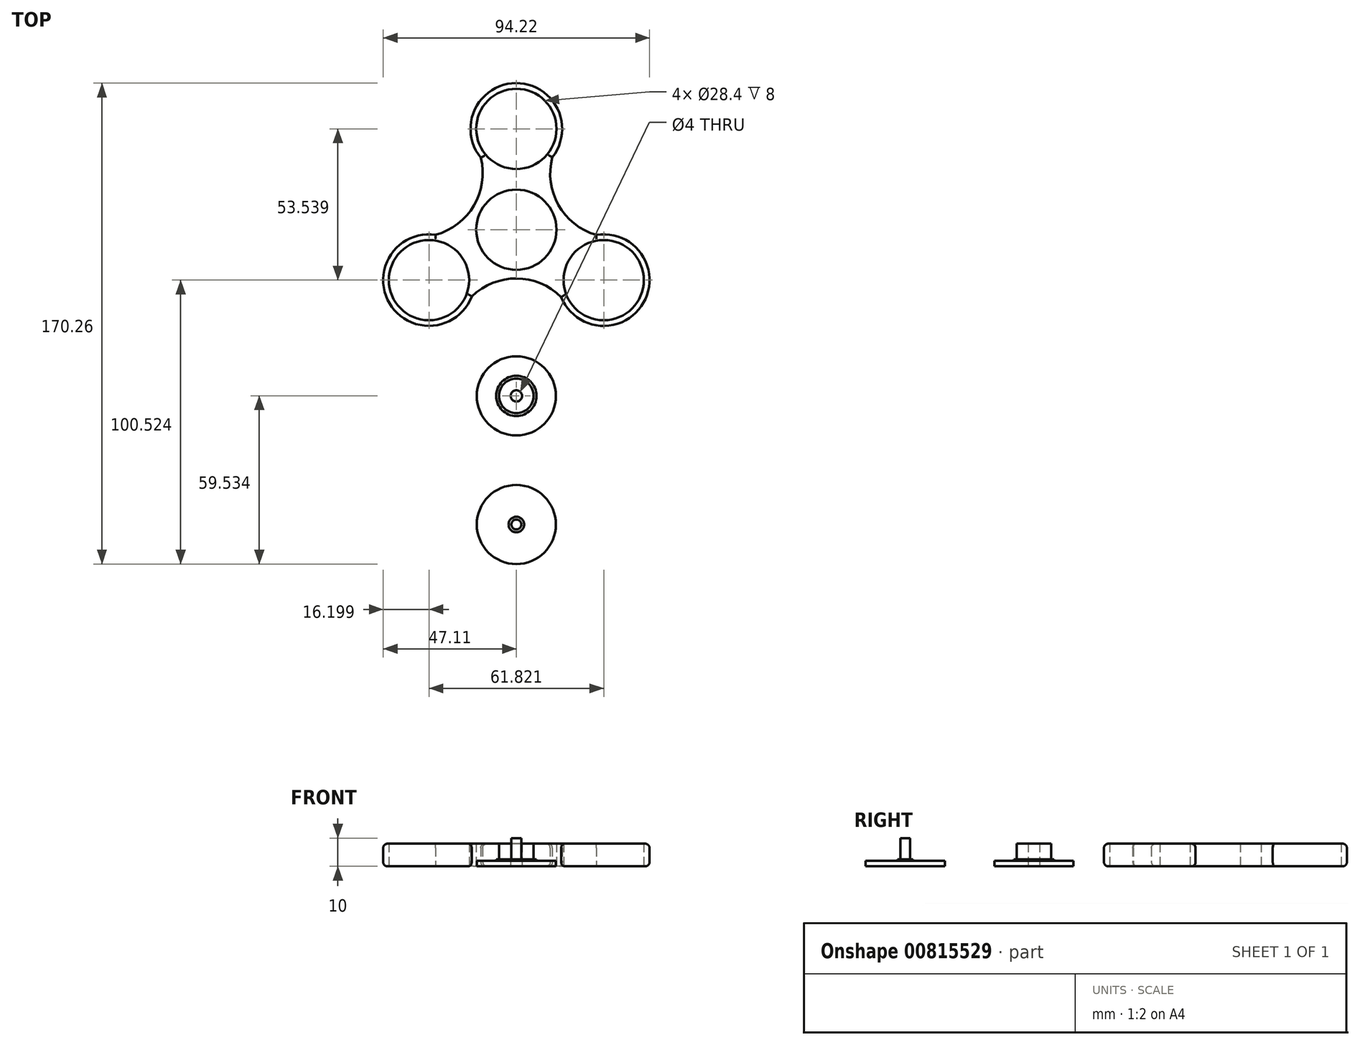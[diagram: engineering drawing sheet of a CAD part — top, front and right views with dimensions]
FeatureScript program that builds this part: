
annotation { "Feature Type Name" : "Feature", "Feature Type Description" : "" }
export const myFeature = defineFeature(function(context is Context, id is Id, definition is map)
    precondition{}
    {
        {
            var Q0;
            Q0=qCreatedBy(makeId("Top.planeOp"),FACE);
            var sketch = newSketch(context, id + "F0", { "sketchPlane" : qUnion([Q0])});
            skCircle(sketch, "E0", {"center": v(0, 0) * mm, "radius": 14.2 * mm});
            skCircle(sketch, "E1", {"center": v(0, 35.7) * mm, "radius": 14.2 * mm});
            skArc(sketch, "E2", {"start": v(12.73, 25.67) * mm, "mid": v(-0.12, 51.9) * mm, "end": v(-12.58, 25.49) * mm});
            skArc(sketch, "E3.1.0", {"start": v(-28.6, -1.81) * mm, "mid": v(-44.88, -26.05) * mm, "end": v(-15.78, -23.64) * mm});
            skCircle(sketch, "E3.1.1", {"center": v(-30.91, -17.85) * mm, "radius": 14.2 * mm});
            skArc(sketch, "E3.2.0", {"start": v(15.87, -23.86) * mm, "mid": v(45, -25.84) * mm, "end": v(28.36, -1.85) * mm});
            skCircle(sketch, "E3.2.1", {"center": v(30.91, -17.85) * mm, "radius": 14.2 * mm});
            skArc(sketch, "E4", {"start": v(15.87, -23.86) * mm, "mid": v(0.09, -17.27) * mm, "end": v(-15.78, -23.64) * mm});
            skArc(sketch, "E5.1.0", {"start": v(12.73, 25.67) * mm, "mid": v(14.9, 8.71) * mm, "end": v(28.36, -1.85) * mm});
            skArc(sketch, "E5.2.0", {"start": v(-28.6, -1.81) * mm, "mid": v(-15, 8.56) * mm, "end": v(-12.58, 25.49) * mm});
            skSolve(sketch);
        }
        {
            var Q0;
            Q0=qSketchRegion(id+"F0",true);
            extrude(context, id + "F1", {"entities" : qUnion([Q0]), "depth" : 8 * mm, "offsetDistance" : 25 * mm});
        }
        {
            var Q0;
            Q0=makeQuery(id+"F1.opExtrude","CAP_EDGE",EDGE,{"disambiguationData":[OSD([sQuery(id+"F0.wireOp",EDGE,"E3.1.0")])],"isStart":false});
            var Q1;
            Q1=makeQuery(id+"F1.opExtrude","CAP_EDGE",EDGE,{"disambiguationData":[OSD([sQuery(id+"F0.wireOp",EDGE,"E4")])],"isStart":false});
            var Q2;
            Q2=makeQuery(id+"F1.opExtrude","CAP_EDGE",EDGE,{"disambiguationData":[OSD([sQuery(id+"F0.wireOp",EDGE,"E3.2.0")])],"isStart":false});
            var Q3;
            Q3=makeQuery(id+"F1.opExtrude","CAP_EDGE",EDGE,{"disambiguationData":[OSD([sQuery(id+"F0.wireOp",EDGE,"E5.1.0")])],"isStart":false});
            var Q4;
            Q4=makeQuery(id+"F1.opExtrude","CAP_EDGE",EDGE,{"disambiguationData":[OSD([sQuery(id+"F0.wireOp",EDGE,"E2")])],"isStart":false});
            var Q5;
            Q5=makeQuery(id+"F1.opExtrude","CAP_EDGE",EDGE,{"disambiguationData":[OSD([sQuery(id+"F0.wireOp",EDGE,"E5.2.0")])],"isStart":false});
            var Q6;
            Q6=makeQuery(id+"F1.opExtrude","CAP_EDGE",EDGE,{"disambiguationData":[OSD([sQuery(id+"F0.wireOp",EDGE,"E4")])],"isStart":true});
            var Q7;
            Q7=makeQuery(id+"F1.opExtrude","CAP_EDGE",EDGE,{"disambiguationData":[OSD([sQuery(id+"F0.wireOp",EDGE,"E3.1.0")])],"isStart":true});
            var Q8;
            Q8=makeQuery(id+"F1.opExtrude","CAP_EDGE",EDGE,{"disambiguationData":[OSD([sQuery(id+"F0.wireOp",EDGE,"E5.2.0")])],"isStart":true});
            var Q9;
            Q9=makeQuery(id+"F1.opExtrude","CAP_EDGE",EDGE,{"disambiguationData":[OSD([sQuery(id+"F0.wireOp",EDGE,"E2")])],"isStart":true});
            var Q10;
            Q10=makeQuery(id+"F1.opExtrude","CAP_EDGE",EDGE,{"disambiguationData":[OSD([sQuery(id+"F0.wireOp",EDGE,"E5.1.0")])],"isStart":true});
            var Q11;
            Q11=makeQuery(id+"F1.opExtrude","CAP_EDGE",EDGE,{"disambiguationData":[OSD([sQuery(id+"F0.wireOp",EDGE,"E3.2.0")])],"isStart":true});
            fillet(context, id + "F2", {"entities" : qUnion([Q0, Q1, Q2, Q3, Q4, Q5, Q6, Q7, Q8, Q9, Q10, Q11]), "radius" : 1.5 * mm, "tangentPropagation" : true, "allowEdgeOverflow" : false});
        }
        {
            var Q0;
            Q0=qCreatedBy(makeId("Right.planeOp"),FACE);
            var sketch = newSketch(context, id + "F3", { "sketchPlane" : qUnion([Q0])});
            skLineSegment(sketch, "E6", {"start": v(-72.84, 0) * mm, "end": v(-72.84, 2) * mm});
            skLineSegment(sketch, "E7", {"start": v(-72.84, 2) * mm, "end": v(-65.95, 2) * mm});
            skLineSegment(sketch, "E8", {"start": v(-58.84, 0) * mm, "end": v(-72.84, 0) * mm});
            skLineSegment(sketch, "E9.top", {"start": v(-64.95, 8) * mm, "end": v(-58.84, 8) * mm});
            skLineSegment(sketch, "E9.left", {"start": v(-64.95, 2.5) * mm, "end": v(-64.95, 8) * mm});
            skPoint(sketch, "E10.start.orphan", {"position": v(-58.84, 0) * mm});
            skLineSegment(sketch, "E11.top", {"start": v(-64.95, 2.5) * mm, "end": v(-65.95, 2.5) * mm});
            skLineSegment(sketch, "E11.right", {"start": v(-65.95, 2) * mm, "end": v(-65.95, 2.5) * mm});
            skLineSegment(sketch, "E12", {"start": v(-58.84, 8) * mm, "end": v(-58.84, 0) * mm});
            skSolve(sketch);
        }
        {
            var Q0;
            Q0=makeQuery(id+"F3.imprint","IMPRINT",FACE,{"disambiguationData":[TD([[makeQuery(id+"F3.imprint","IMPRINT",EDGE,{"derivedFrom":sQuery(id+"F3.wireOp",EDGE,"E6")}),-1.0]])]});
            var Q1;
            Q1=sQuery(id+"F3.wireOp",EDGE,"E12");
            revolve(context, id + "F4", {"surfaceOperationType" : NewSurfaceOperationType.NEW, "entities" : qUnion([Q0]), "axis" : qUnion([Q1]), "revolveType" : RevolveType.FULL});
        }
        {
            var Q0;
            Q0=makeQuery(id+"F4.opRevolve","SWEPT_FACE",FACE,{"disambiguationData":[OSD([sQuery(id+"F3.wireOp",EDGE,"E8")])]});
            var sketch = newSketch(context, id + "F5", { "sketchPlane" : qUnion([Q0])});
            skPoint(sketch, "E13", {"position": v(0, 58.84) * mm});
            skSolve(sketch);
        }
        {
            var Q0;
            Q0=sQuery(id+"F5.wireOp",VERTEX,"E13");
            var Q1;
            Q1=makeQuery(id+"F4.opRevolve","SWEPT_BODY",BODY,{"disambiguationData":[OSD([sQuery(id+"F3.wireOp",EDGE,"E6"),sQuery(id+"F3.wireOp",EDGE,"E7"),sQuery(id+"F3.wireOp",EDGE,"E8"),sQuery(id+"F3.wireOp",EDGE,"E9.top"),sQuery(id+"F3.wireOp",EDGE,"E9.left"),sQuery(id+"F3.wireOp",EDGE,"E11.top"),sQuery(id+"F3.wireOp",EDGE,"E11.right"),sQuery(id+"F3.wireOp",EDGE,"E12")])]});
            hole(context, id + "F6", {"style" : HoleStyle.SIMPLE, "endStyle" : HoleEndStyle.THROUGH, "holeDiameter" : 4 * mm, "majorDiameter" : 5 * mm, "isTappedThrough" : true, "tappedDepth" : 12 * mm, "tapClearance" : 3, "startFromSketch" : true, "locations" : qUnion([Q0]), "scope" : qUnion([Q1])});
        }
        {
            var Q0;
            Q0=qCreatedBy(makeId("Right.planeOp"),FACE);
            var sketch = newSketch(context, id + "F7", { "sketchPlane" : qUnion([Q0])});
            skLineSegment(sketch, "E14", {"start": v(-118.37, 0) * mm, "end": v(-104.37, 0) * mm});
            skLineSegment(sketch, "E15", {"start": v(-104.37, 0) * mm, "end": v(-104.37, 10) * mm});
            skLineSegment(sketch, "E16", {"start": v(-104.37, 10) * mm, "end": v(-106.12, 10) * mm});
            skLineSegment(sketch, "E17", {"start": v(-106.12, 10) * mm, "end": v(-106.12, 2.5) * mm});
            skLineSegment(sketch, "E18", {"start": v(-106.12, 2.5) * mm, "end": v(-107.12, 2.5) * mm});
            skLineSegment(sketch, "E19", {"start": v(-107.12, 2.5) * mm, "end": v(-107.12, 2) * mm});
            skLineSegment(sketch, "E20", {"start": v(-118.37, 0) * mm, "end": v(-118.37, 2) * mm});
            skLineSegment(sketch, "E21", {"start": v(-118.37, 2) * mm, "end": v(-107.12, 2) * mm});
            skSolve(sketch);
        }
        {
            var Q0;
            Q0=qSketchRegion(id+"F7",true);
            var Q1;
            Q1=sQuery(id+"F7.wireOp",EDGE,"E15");
            revolve(context, id + "F8", {"surfaceOperationType" : NewSurfaceOperationType.NEW, "entities" : qUnion([Q0]), "axis" : qUnion([Q1]), "revolveType" : RevolveType.FULL});
        }
    });
